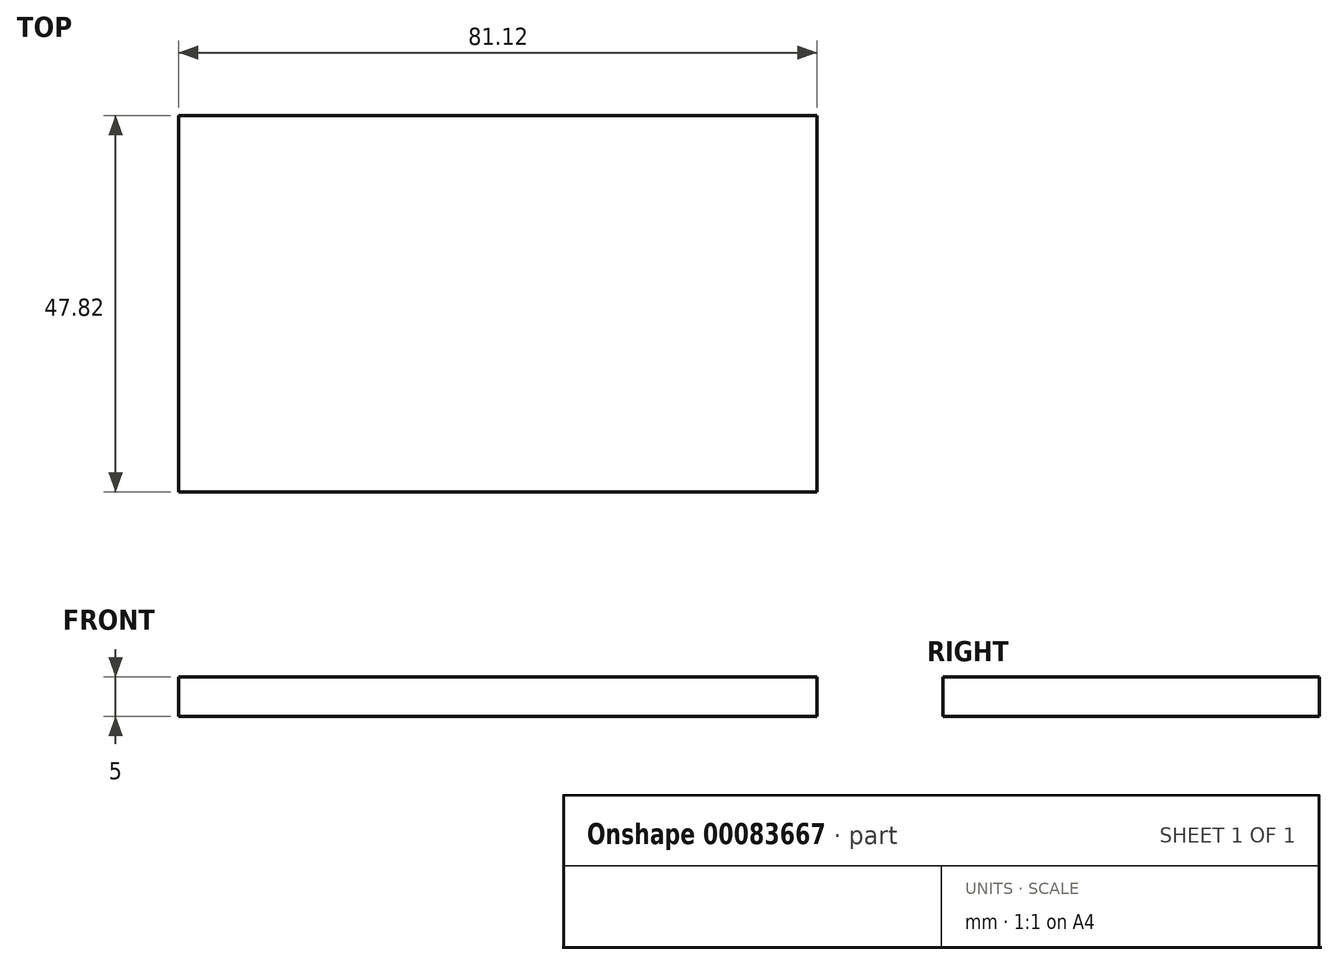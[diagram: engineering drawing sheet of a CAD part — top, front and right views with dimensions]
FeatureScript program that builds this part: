
annotation { "Feature Type Name" : "Feature", "Feature Type Description" : "" }
export const myFeature = defineFeature(function(context is Context, id is Id, definition is map)
    precondition{}
    {
        {
            var Q0;
            Q0=qCreatedBy(makeId("Top.planeOp"),FACE);
            var sketch = newSketch(context, id + "F0", { "sketchPlane" : qUnion([Q0])});
            skLineSegment(sketch, "E0.bottom", {"start": v(-40.56, 23.91) * mm, "end": v(40.56, 23.91) * mm});
            skLineSegment(sketch, "E0.top", {"start": v(-40.56, -23.91) * mm, "end": v(40.56, -23.91) * mm});
            skLineSegment(sketch, "E0.left", {"start": v(-40.56, 23.91) * mm, "end": v(-40.56, -23.91) * mm});
            skLineSegment(sketch, "E0.right", {"start": v(40.56, 23.91) * mm, "end": v(40.56, -23.91) * mm});
            skPoint(sketch, "E0.middle", {"position": v(0, 0) * mm});
            skSolve(sketch);
        }
        {
            var Q0;
            Q0 = qSketchRegion(id + "F0", true);
            extrude(context, id + "F1", {"entities" : qUnion([Q0]), "depth" : 5 * mm});
        }
    });
